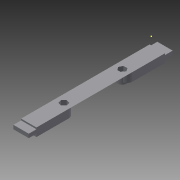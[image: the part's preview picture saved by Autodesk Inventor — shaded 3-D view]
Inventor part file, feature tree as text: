
AUTODESK INVENTOR PART (.ipt)
format: ipt  version: 2015 (Build 190159000, 159)  size: 202,240 bytes
history: native  units: in
note: dims shown in document units (in); Inventor stores cm internally (conversion verified against a paired STEP export)
features: sketch x8, extrude x7, projected_geometry x7, reference x2, chamfer x1, fillet x1
ambient origin geometry x8: Origin, YZ Plane, XZ Plane, XY Plane, X Axis, Y Axis, Z Axis, Center Point
bodies: Solid1 (feature_tree)
feature tree (26):
  extrude  "Extrusion1"  Depth=1.0in
  extrude  "Extrusion2"  Depth=0.25in
  extrude  "Extrusion3"  Depth=4.8in TaperAngle=0.0deg
  extrude  "Extrusion4"  Depth=0.1in TaperAngle=0.0deg
  chamfer  "Chamfer1"  Distance=0.0625in
  fillet  "Fillet1"  Radius=0.375in
  sketch  "Sketch7"  dims[d19=0.4375in d20=0.3in d21=0.0in]
  extrude  "Extrusion6"  Depth=0.3in TaperAngle=0.0deg
  extrude  "Extrusion5"  Depth=0.624in
  extrude  "Extrusion7"  [1 undecoded]
  sketch  "Sketch1"  dims[d0=1.0in d1=0.25in]
  sketch  "Sketch2"  dims[d2=9.3625in d3=0.0in d6=0.25in]
  projected_geometry  "Projected Loop1"
  sketch  "Sketch3"  dims[d7=0.25in d8=4.8in d9=0.0in]
  reference  "Reference1"
  reference  "Reference2"
  projected_geometry  "Projected Loop2"
  sketch  "Sketch5"  dims[d10=3.8in d11=0.1in d12=0.0in d13=0.0625in d14=0.0in]
  projected_geometry  "Projected Loop4"
  sketch  "Sketch6"  dims[d15=0.25in d16=0.9375in d17=45.0deg d18=0.375in]
  projected_geometry  "Projected Loop5"
  sketch  "Sketch8"  dims[d22=0.6562in d23=0.0in d24=0.624in]
  projected_geometry  "Projected Loop6"
  sketch  "Sketch9"  dims[d25=0.1875in d26=0.0in]
  projected_geometry  "Projected Loop7"
  projected_geometry  "Projected Loop8"
note: 1 required parameter value undecoded (feature->parameter linkage not recoverable at this tier; creation-order binding heuristic only, values carry confidence <= 0.55)
